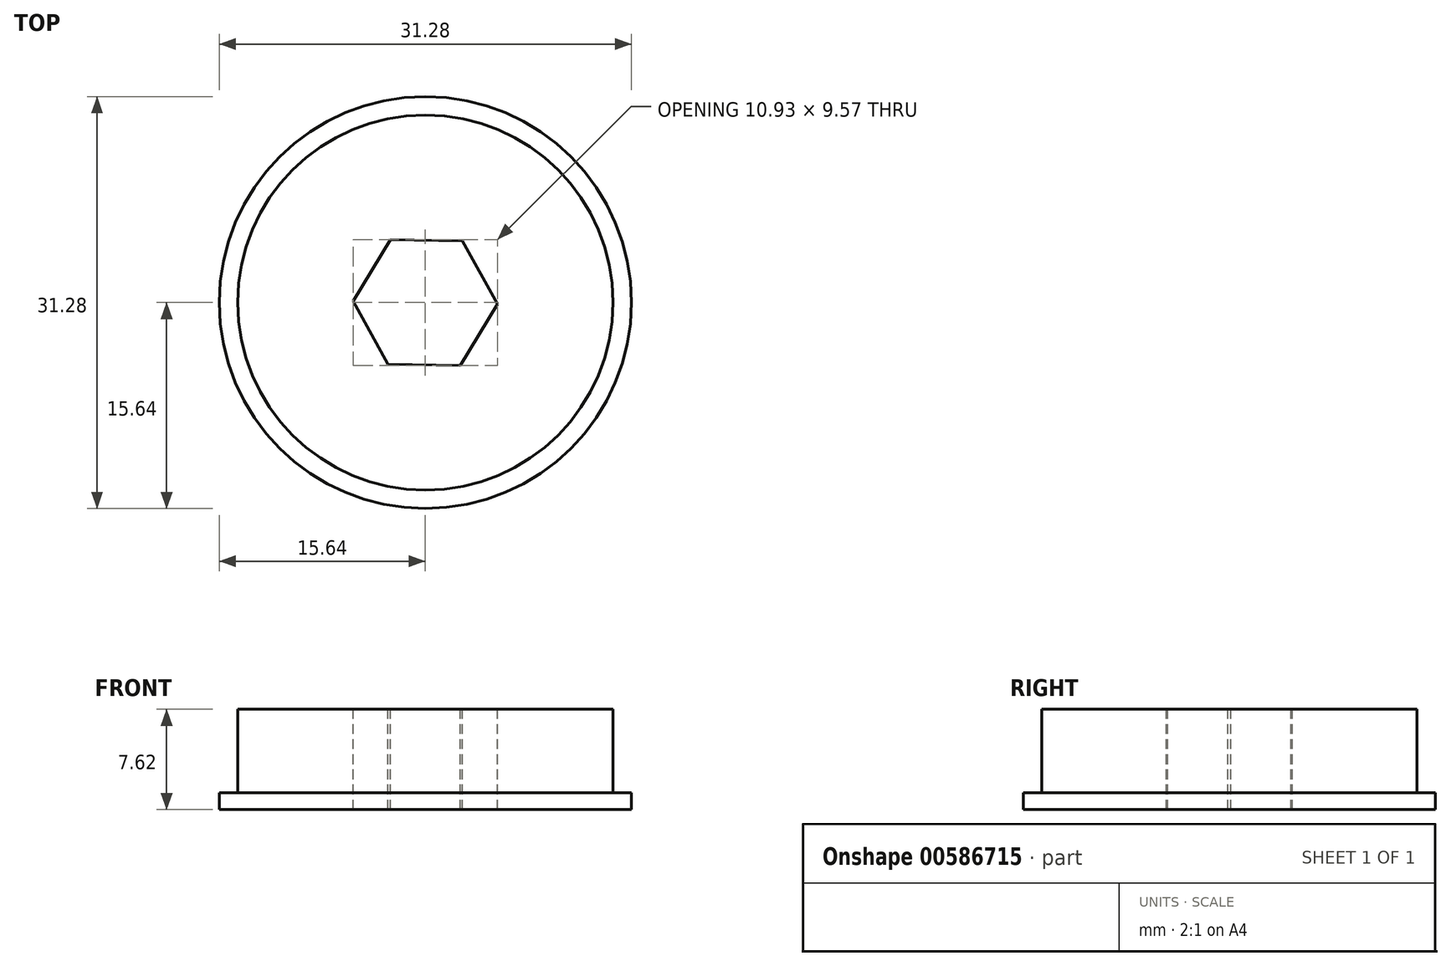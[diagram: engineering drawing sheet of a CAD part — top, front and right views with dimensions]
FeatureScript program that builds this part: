
annotation { "Feature Type Name" : "Feature", "Feature Type Description" : "" }
export const myFeature = defineFeature(function(context is Context, id is Id, definition is map)
    precondition{}
    {
        {
            var Q0;
            Q0=qCreatedBy(makeId("Top.planeOp"),FACE);
            var sketch = newSketch(context, id + "F0", { "sketchPlane" : qUnion([Q0])});
            skCircle(sketch, "E0", {"center": v(0, 0) * mm, "radius": 15.64 * mm});
            skSolve(sketch);
        }
        {
            var Q0;
            Q0=makeQuery(id+"F0.imprint","IMPRINT",FACE,{"disambiguationData":[TD([[makeQuery(id+"F0.imprint","IMPRINT",EDGE,{"derivedFrom":sQuery(id+"F0.wireOp",EDGE,"E0")}),1.0]])]});
            extrude(context, id + "F1", {"entities" : qUnion([Q0]), "depth" : 1.27 * mm, "offsetDistance" : 25.4 * mm});
        }
        {
            var Q0;
            Q0=makeQuery(id+"F1.opExtrude","CAP_FACE",FACE,{"disambiguationData":[OSD([sQuery(id+"F0.wireOp",EDGE,"E0")])],"isStart":false});
            var sketch = newSketch(context, id + "F2", { "sketchPlane" : qUnion([Q0])});
            skCircle(sketch, "E1", {"center": v(0, 0) * mm, "radius": 14.25 * mm});
            skSolve(sketch);
        }
        {
            var Q0;
            Q0=makeQuery(id+"F2.imprint","IMPRINT",FACE,{"disambiguationData":[TD([[makeQuery(id+"F2.imprint","IMPRINT",EDGE,{"derivedFrom":sQuery(id+"F2.wireOp",EDGE,"E1")}),1.0]])]});
            extrude(context, id + "F3", {"entities" : qUnion([Q0]), "operationType" : NewBodyOperationType.ADD, "depth" : 6.35 * mm, "offsetDistance" : 25.4 * mm});
        }
        {
            var Q0;
            Q0=makeQuery(id+"F3.opExtrude","CAP_FACE",FACE,{"disambiguationData":[OSD([sQuery(id+"F2.wireOp",EDGE,"E1")])],"isStart":false});
            var sketch = newSketch(context, id + "F4", { "sketchPlane" : qUnion([Q0])});
            skCircle(sketch, "E2.cCircle", {"center": v(0, 0) * mm, "radius": 4.73 * mm, "construction": true});
            skLineSegment(sketch, "E2.0", {"start": v(2.83, 4.68) * mm, "end": v(5.47, -0.1) * mm});
            skLineSegment(sketch, "E2.1", {"start": v(5.47, -0.1) * mm, "end": v(2.64, -4.79) * mm});
            skLineSegment(sketch, "E2.2", {"start": v(2.64, -4.79) * mm, "end": v(-2.83, -4.68) * mm});
            skLineSegment(sketch, "E2.3", {"start": v(-2.83, -4.68) * mm, "end": v(-5.47, 0.1) * mm});
            skLineSegment(sketch, "E2.4", {"start": v(-5.47, 0.1) * mm, "end": v(-2.64, 4.79) * mm});
            skLineSegment(sketch, "E2.5", {"start": v(-2.64, 4.79) * mm, "end": v(2.83, 4.68) * mm});
            skPoint(sketch, "E2.0.midPoint", {"position": v(4.15, 2.29) * mm});
            skCircle(sketch, "E3", {"center": v(0, 0) * mm, "radius": 6.53 * mm});
            skCircle(sketch, "E4", {"center": v(0, 0) * mm, "radius": 13.2 * mm});
            skSolve(sketch);
        }
        {
            var Q0;
            Q0=makeQuery(id+"F4.imprint","IMPRINT",FACE,{"disambiguationData":[TD([[makeQuery(id+"F4.imprint","IMPRINT",EDGE,{"derivedFrom":sQuery(id+"F4.wireOp",EDGE,"E2.0")}),-1.0]])]});
            extrude(context, id + "F5", {"entities" : qUnion([Q0]), "operationType" : NewBodyOperationType.REMOVE, "oppositeDirection" : true, "depth" : 25.4 * mm, "offsetDistance" : 25.4 * mm});
        }
    });
